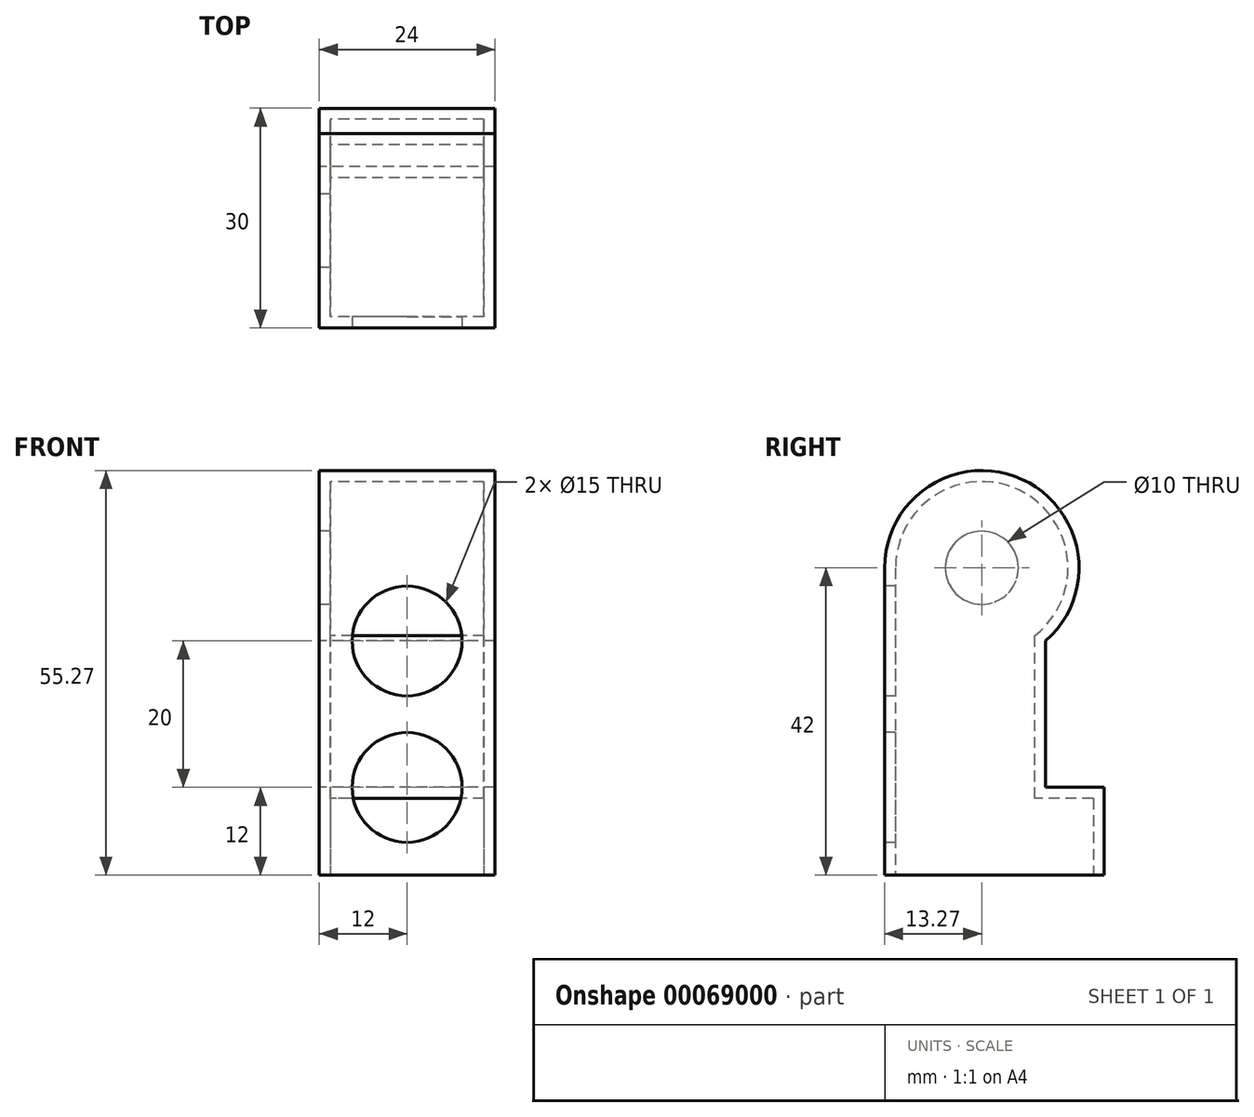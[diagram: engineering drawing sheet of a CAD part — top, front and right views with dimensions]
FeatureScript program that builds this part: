
annotation { "Feature Type Name" : "Feature", "Feature Type Description" : "" }
export const myFeature = defineFeature(function(context is Context, id is Id, definition is map)
    precondition{}
    {
        {
            var Q0;
            Q0=qCreatedBy(makeId("Right.planeOp"),FACE);
            var sketch = newSketch(context, id + "F0", { "sketchPlane" : qUnion([Q0])});
            skArc(sketch, "E0", {"start": v(8.73, -10) * mm, "mid": v(5.5, 12.08) * mm, "end": v(-13.27, 0) * mm});
            skLineSegment(sketch, "E1", {"start": v(-13.27, 0) * mm, "end": v(-13.27, -42) * mm});
            skLineSegment(sketch, "E2", {"start": v(-13.27, -42) * mm, "end": v(16.73, -42) * mm});
            skLineSegment(sketch, "E3", {"start": v(16.73, -30) * mm, "end": v(16.73, -42) * mm});
            skLineSegment(sketch, "E4", {"start": v(16.73, -30) * mm, "end": v(8.73, -30) * mm});
            skLineSegment(sketch, "E5", {"start": v(8.73, -30) * mm, "end": v(8.73, -10) * mm});
            skSolve(sketch);
        }
        {
            var Q0;
            Q0=makeQuery(id+"F0.imprint","IMPRINT",FACE,{"disambiguationData":[TD([[makeQuery(id+"F0.imprint","IMPRINT",EDGE,{"derivedFrom":sQuery(id+"F0.wireOp",EDGE,"E0")}),1.0]])]});
            extrude(context, id + "F1", {"entities" : qUnion([Q0]), "depth" : 24 * mm});
        }
        {
            var Q0;
            Q0=makeQuery(id+"F1.opExtrude","SWEPT_FACE",FACE,{"disambiguationData":[OSD([sQuery(id+"F0.wireOp",EDGE,"E2")])]});
            shell(context, id + "F2", {"entities" : qUnion([Q0]), "thickness" : 1.5 * mm});
        }
        {
            var Q0;
            Q0=makeQuery(id+"F1.opExtrude","CAP_FACE",FACE,{"disambiguationData":[OSD([sQuery(id+"F0.wireOp",EDGE,"E0"),sQuery(id+"F0.wireOp",EDGE,"E1"),sQuery(id+"F0.wireOp",EDGE,"E2"),sQuery(id+"F0.wireOp",EDGE,"E3"),sQuery(id+"F0.wireOp",EDGE,"E4"),sQuery(id+"F0.wireOp",EDGE,"E5")])],"isStart":true});
            var sketch = newSketch(context, id + "F3", { "sketchPlane" : qUnion([Q0])});
            skCircle(sketch, "E6", {"center": v(0, 0) * mm, "radius": 5 * mm});
            skSolve(sketch);
        }
        {
            var Q0;
            Q0 = qSketchRegion(id + "F3", true);
            extrude(context, id + "F4", {"entities" : qUnion([Q0]), "operationType" : NewBodyOperationType.REMOVE, "oppositeDirection" : true, "depth" : 5 * mm});
        }
        {
            var Q0;
            Q0=makeQuery(id+"F1.opExtrude","SWEPT_FACE",FACE,{"disambiguationData":[OSD([sQuery(id+"F0.wireOp",EDGE,"E1")])]});
            var sketch = newSketch(context, id + "F5", { "sketchPlane" : qUnion([Q0])});
            skCircle(sketch, "E7", {"center": v(12, -10) * mm, "radius": 7.5 * mm});
            skCircle(sketch, "E8", {"center": v(12, -30) * mm, "radius": 7.5 * mm});
            skSolve(sketch);
        }
        {
            var Q0;
            Q0 = qSketchRegion(id + "F5", true);
            extrude(context, id + "F6", {"entities" : qUnion([Q0]), "operationType" : NewBodyOperationType.REMOVE, "oppositeDirection" : true, "depth" : 5 * mm});
        }
    });
